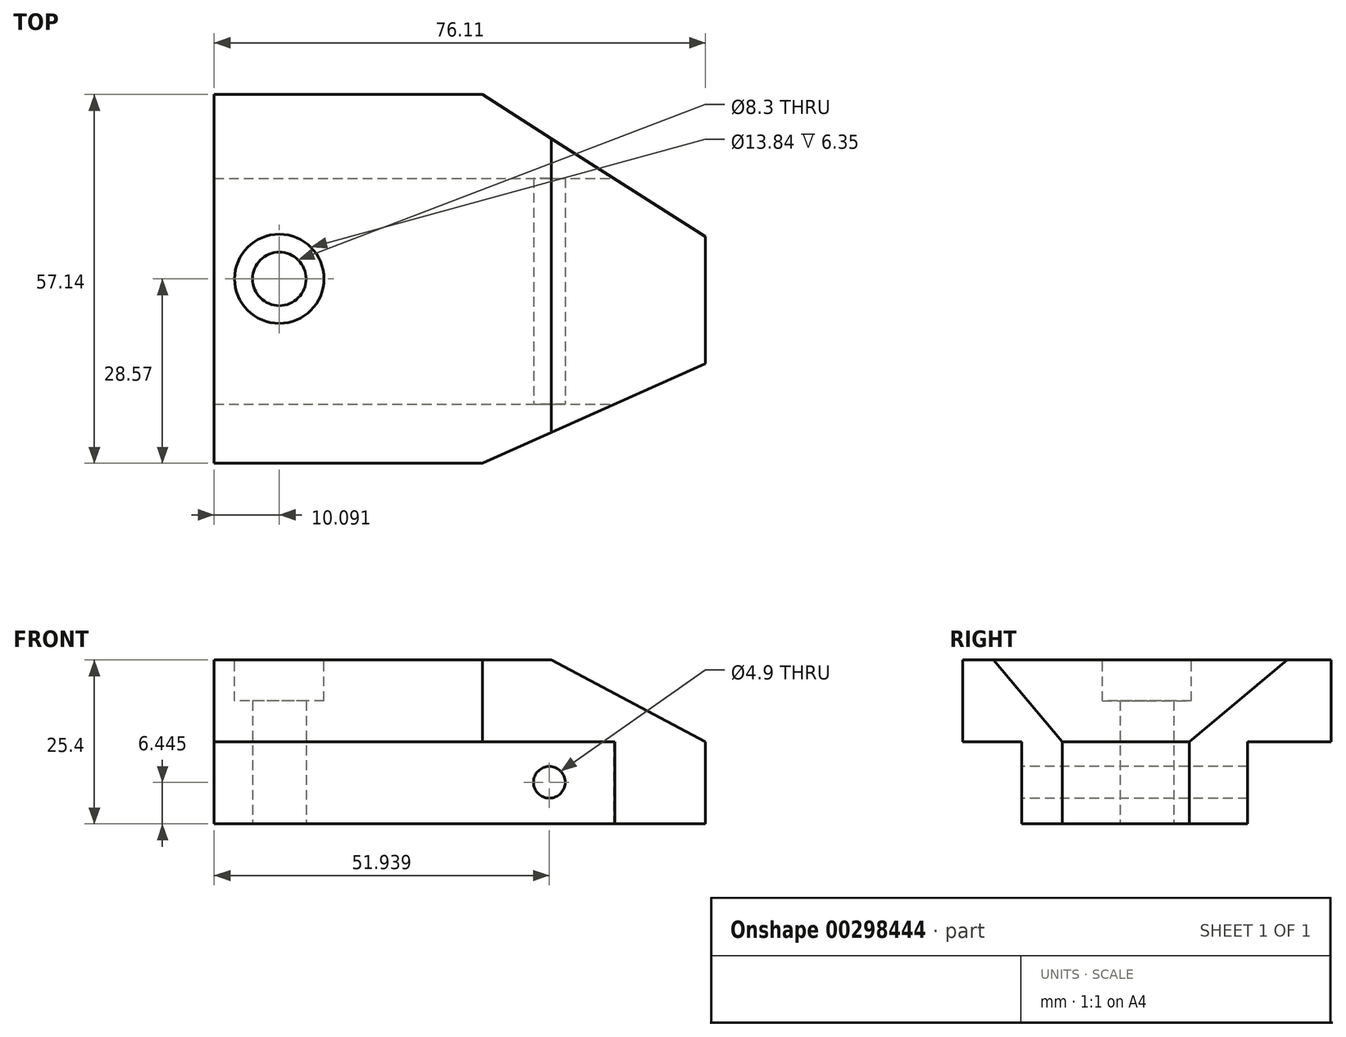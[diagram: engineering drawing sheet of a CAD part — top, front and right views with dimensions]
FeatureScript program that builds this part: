
annotation { "Feature Type Name" : "Feature", "Feature Type Description" : "" }
export const myFeature = defineFeature(function(context is Context, id is Id, definition is map)
    precondition{}
    {
        {
            var Q0;
            Q0=qCreatedBy(makeId("Top.planeOp"),FACE);
            var sketch = newSketch(context, id + "F0", { "sketchPlane" : qUnion([Q0])});
            skLineSegment(sketch, "E0.bottom", {"start": v(-20.78, 28.57) * mm, "end": v(20.78, 28.57) * mm});
            skLineSegment(sketch, "E0.top", {"start": v(-20.78, -28.57) * mm, "end": v(20.78, -28.57) * mm});
            skLineSegment(sketch, "E0.left", {"start": v(-20.78, 28.57) * mm, "end": v(-20.78, -28.57) * mm});
            skPoint(sketch, "E0.middle", {"position": v(0, 0) * mm});
            skLineSegment(sketch, "E1", {"start": v(20.78, 28.57) * mm, "end": v(55.33, 6.54) * mm});
            skLineSegment(sketch, "E2", {"start": v(20.78, -28.57) * mm, "end": v(55.33, -13.14) * mm});
            skLineSegment(sketch, "E3", {"start": v(55.33, -13.14) * mm, "end": v(55.33, 6.54) * mm});
            skCircle(sketch, "E4", {"center": v(-10.69, 0) * mm, "radius": 4.15 * mm});
            skSolve(sketch);
        }
        {
            var Q0;
            Q0 = qSketchRegion(id + "F0", true);
            extrude(context, id + "F1", {"entities" : qUnion([Q0]), "depth" : 25.4 * mm});
        }
        {
            var Q0;
            Q0=qCreatedBy(makeId("Front.planeOp"),FACE);
            var sketch = newSketch(context, id + "F2", { "sketchPlane" : qUnion([Q0])});
            skLineSegment(sketch, "E5", {"start": v(55.33, 12.7) * mm, "end": v(55.33, 25.4) * mm});
            skLineSegment(sketch, "E6", {"start": v(55.33, 25.4) * mm, "end": v(31.46, 25.4) * mm});
            skLineSegment(sketch, "E7", {"start": v(31.46, 25.4) * mm, "end": v(55.33, 12.7) * mm});
            skSolve(sketch);
        }
        {
            var Q0;
            Q0 = qSketchRegion(id + "F2", true);
            extrude(context, id + "F3", {"entities" : qUnion([Q0]), "operationType" : NewBodyOperationType.REMOVE, "endBound" : BoundingType.SYMMETRIC, "oppositeDirection" : true, "depth" : 101.6 * mm});
        }
        {
            var Q0;
            Q0=makeQuery(id+"F1.opExtrude","CAP_FACE",FACE,{"disambiguationData":[OSD([sQuery(id+"F0.wireOp",EDGE,"E0.bottom"),sQuery(id+"F0.wireOp",EDGE,"E0.top"),sQuery(id+"F0.wireOp",EDGE,"E0.left"),sQuery(id+"F0.wireOp",EDGE,"E1"),sQuery(id+"F0.wireOp",EDGE,"E2"),sQuery(id+"F0.wireOp",EDGE,"E3"),sQuery(id+"F0.wireOp",EDGE,"E4")])],"isStart":true});
            var sketch = newSketch(context, id + "F4", { "sketchPlane" : qUnion([Q0])});
            skLineSegment(sketch, "E8.bottom", {"start": v(-20.78, 28.57) * mm, "end": v(41.32, 28.57) * mm});
            skLineSegment(sketch, "E8.top", {"start": v(-20.78, 19.4) * mm, "end": v(41.32, 19.4) * mm});
            skLineSegment(sketch, "E8.left", {"start": v(-20.78, 28.57) * mm, "end": v(-20.78, 19.4) * mm});
            skLineSegment(sketch, "E8.right", {"start": v(41.32, 28.57) * mm, "end": v(41.32, 19.4) * mm});
            skLineSegment(sketch, "E9.bottom", {"start": v(-20.78, -28.57) * mm, "end": v(41.12, -28.57) * mm});
            skLineSegment(sketch, "E9.top", {"start": v(-20.78, -15.6) * mm, "end": v(41.12, -15.6) * mm});
            skLineSegment(sketch, "E9.left", {"start": v(-20.78, -28.57) * mm, "end": v(-20.78, -15.6) * mm});
            skLineSegment(sketch, "E9.right", {"start": v(41.12, -28.57) * mm, "end": v(41.12, -15.6) * mm});
            skSolve(sketch);
        }
        {
            var Q0;
            {var subQ4=sQuery(id+"F4.wireOp",EDGE,"E8.top");Q0=makeQuery(id+"F4.imprint","IMPRINT",FACE,{"disambiguationData":[TD([[makeQuery(id+"F4.imprint","IMPRINT",EDGE,{"derivedFrom":subQ4}),1.0]])]});}
            var Q1;
            {var subQ4=sQuery(id+"F4.wireOp",EDGE,"E9.top");Q1=makeQuery(id+"F4.imprint","IMPRINT",FACE,{"disambiguationData":[TD([[makeQuery(id+"F4.imprint","IMPRINT",EDGE,{"derivedFrom":subQ4}),-1.0]])]});}
            extrude(context, id + "F5", {"entities" : qUnion([Q0, Q1]), "operationType" : NewBodyOperationType.REMOVE, "oppositeDirection" : true, "depth" : 12.7 * mm});
        }
        {
            var Q0;
            Q0=makeQuery(id+"F1.opExtrude","CAP_FACE",FACE,{"disambiguationData":[OSD([sQuery(id+"F0.wireOp",EDGE,"E0.bottom"),sQuery(id+"F0.wireOp",EDGE,"E0.top"),sQuery(id+"F0.wireOp",EDGE,"E0.left"),sQuery(id+"F0.wireOp",EDGE,"E1"),sQuery(id+"F0.wireOp",EDGE,"E2"),sQuery(id+"F0.wireOp",EDGE,"E3"),sQuery(id+"F0.wireOp",EDGE,"E4")])],"isStart":false});
            var sketch = newSketch(context, id + "F6", { "sketchPlane" : qUnion([Q0])});
            skCircle(sketch, "E10", {"center": v(-10.69, 0) * mm, "radius": 6.92 * mm});
            skSolve(sketch);
        }
        {
            var Q0;
            Q0 = qSketchRegion(id + "F6", true);
            extrude(context, id + "F7", {"entities" : qUnion([Q0]), "operationType" : NewBodyOperationType.REMOVE, "oppositeDirection" : true, "depth" : 6.35 * mm});
        }
        {
            var Q0;
            Q0=makeQuery(id+"F5.boolean.opBoolean","COPY",FACE,{"derivedFrom":makeQuery(id+"F5.opExtrude","SWEPT_FACE",FACE,{"disambiguationData":[OSD([sQuery(id+"F4.wireOp",EDGE,"E8.top")])]})});
            var sketch = newSketch(context, id + "F8", { "sketchPlane" : qUnion([Q0])});
            skCircle(sketch, "E11", {"center": v(31.16, 6.44) * mm, "radius": 2.45 * mm});
            skSolve(sketch);
        }
        {
            var Q0;
            Q0=makeQuery(id+"F8.imprint","IMPRINT",FACE,{"disambiguationData":[TD([[makeQuery(id+"F8.imprint","IMPRINT",EDGE,{"derivedFrom":sQuery(id+"F8.wireOp",EDGE,"E11")}),1.0]])]});
            extrude(context, id + "F9", {"entities" : qUnion([Q0]), "operationType" : NewBodyOperationType.REMOVE, "endBound" : BoundingType.THROUGH_ALL, "oppositeDirection" : true, "depth" : 25.4 * mm});
        }
    });
